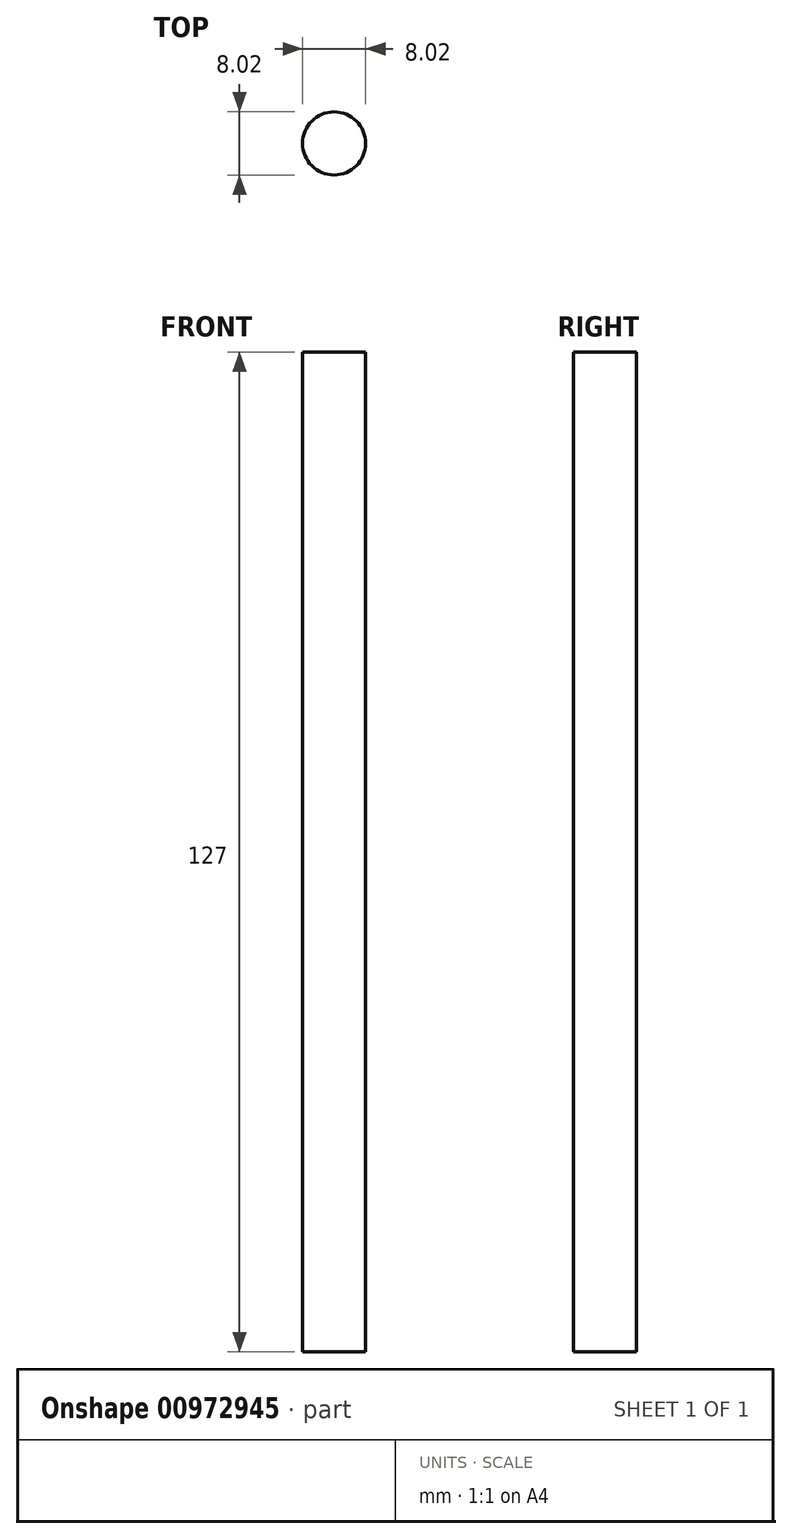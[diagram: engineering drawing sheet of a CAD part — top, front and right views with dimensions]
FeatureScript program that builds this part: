
annotation { "Feature Type Name" : "Feature", "Feature Type Description" : "" }
export const myFeature = defineFeature(function(context is Context, id is Id, definition is map)
    precondition{}
    {
        {
            var Q0;
            Q0=qCreatedBy(makeId("Top.planeOp"),FACE);
            var sketch = newSketch(context, id + "F0", { "sketchPlane" : qUnion([Q0])});
            skCircle(sketch, "E0", {"center": v(0, 0) * mm, "radius": 4 * mm});
            skSolve(sketch);
        }
        {
            var Q0;
            Q0=makeQuery(id+"F0.imprint","IMPRINT",FACE,{"disambiguationData":[TD([[makeQuery(id+"F0.imprint","IMPRINT",EDGE,{"derivedFrom":sQuery(id+"F0.wireOp",EDGE,"E0")}),1.0]])]});
            extrude(context, id + "F1", {"entities" : qUnion([Q0]), "depth" : 127 * mm});
        }
    });
